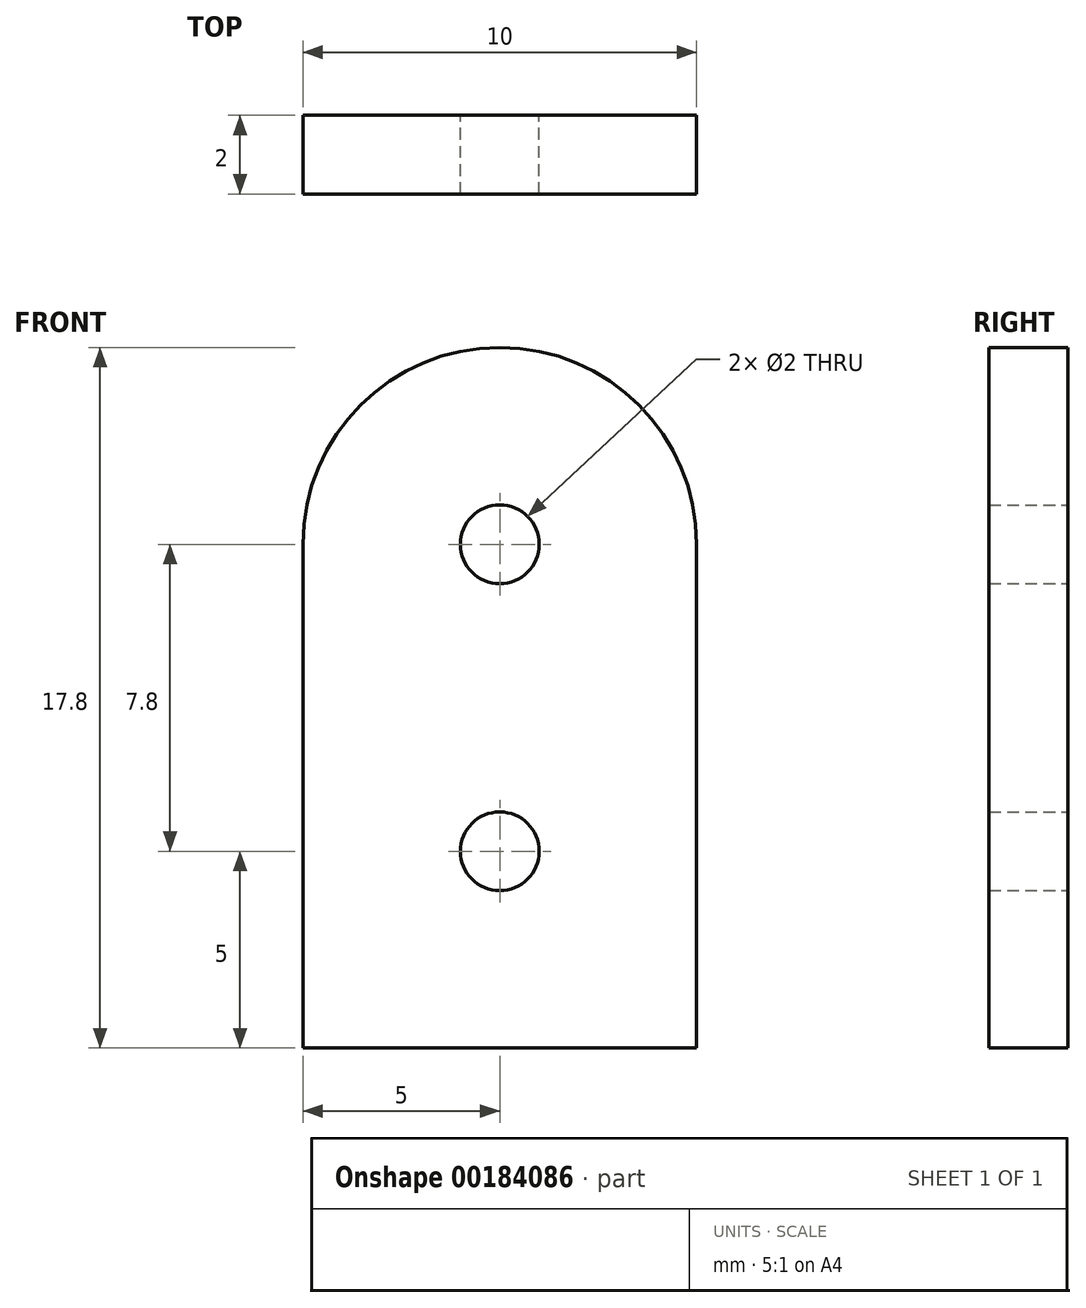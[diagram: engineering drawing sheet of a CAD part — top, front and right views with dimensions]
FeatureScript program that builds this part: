
annotation { "Feature Type Name" : "Feature", "Feature Type Description" : "" }
export const myFeature = defineFeature(function(context is Context, id is Id, definition is map)
    precondition{}
    {
        {
            var Q0;
            Q0=qCreatedBy(makeId("Front.planeOp"),FACE);
            var sketch = newSketch(context, id + "F0", { "sketchPlane" : qUnion([Q0])});
            skLineSegment(sketch, "E0.bottom", {"start": v(0, 0) * mm, "end": v(10, 0) * mm});
            skLineSegment(sketch, "E0.left", {"start": v(0, 0) * mm, "end": v(0, 12.8) * mm});
            skLineSegment(sketch, "E0.right", {"start": v(10, 0) * mm, "end": v(10, 12.8) * mm});
            skArc(sketch, "E1", {"start": v(10, 12.8) * mm, "mid": v(5, 17.8) * mm, "end": v(0, 12.8) * mm});
            skCircle(sketch, "E2", {"center": v(5, 12.8) * mm, "radius": 1 * mm});
            skCircle(sketch, "E3", {"center": v(5, 5) * mm, "radius": 1 * mm});
            skSolve(sketch);
        }
        {
            var Q0;
            Q0=makeQuery(id+"F0.imprint","IMPRINT",FACE,{"disambiguationData":[TD([[makeQuery(id+"F0.imprint","IMPRINT",EDGE,{"derivedFrom":sQuery(id+"F0.wireOp",EDGE,"E0.bottom")}),1.0]])]});
            extrude(context, id + "F1", {"entities" : qUnion([Q0]), "depth" : 2 * mm});
        }
    });
